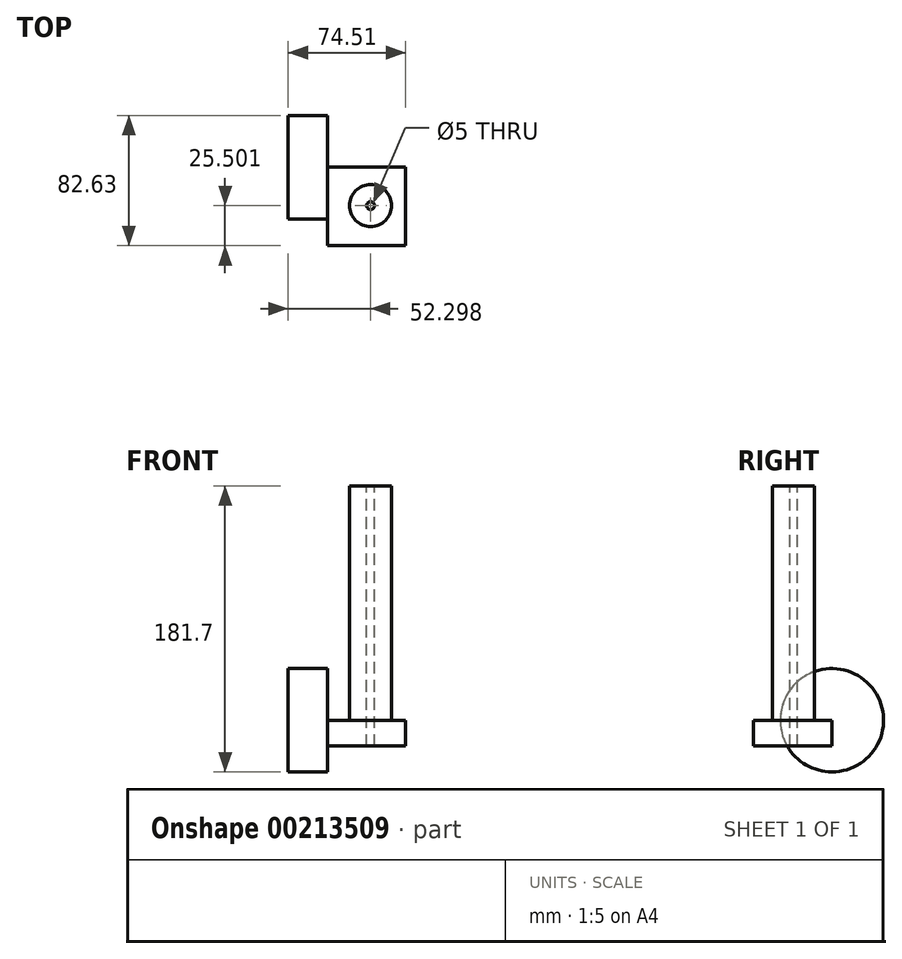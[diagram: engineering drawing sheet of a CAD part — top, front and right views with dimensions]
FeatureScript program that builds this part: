
annotation { "Feature Type Name" : "Feature", "Feature Type Description" : "" }
export const myFeature = defineFeature(function(context is Context, id is Id, definition is map)
    precondition{}
    {
        {
            var Q0;
            Q0=qCreatedBy(makeId("Right.planeOp"),FACE);
            var sketch = newSketch(context, id + "F0", { "sketchPlane" : qUnion([Q0])});
            skCircle(sketch, "E0", {"center": v(-28.06, 48.43) * mm, "radius": 32.8 * mm});
            skSolve(sketch);
        }
        {
            var Q0;
            Q0 = qSketchRegion(id + "F0", true);
            extrude(context, id + "F1", {"entities" : qUnion([Q0]), "depth" : 25 * mm});
        }
        {
            var Q0;
            Q0=makeQuery(id+"F1.opExtrude","CAP_FACE",FACE,{"disambiguationData":[OSD([sQuery(id+"F0.wireOp",EDGE,"E0")])],"isStart":false});
            var sketch = newSketch(context, id + "F2", { "sketchPlane" : qUnion([Q0])});
            skLineSegment(sketch, "E1.bottom", {"start": v(-28.06, 48.43) * mm, "end": v(-77.88, 48.43) * mm});
            skLineSegment(sketch, "E1.top", {"start": v(-28.06, 32) * mm, "end": v(-77.88, 32) * mm});
            skLineSegment(sketch, "E1.left", {"start": v(-28.06, 48.43) * mm, "end": v(-28.06, 32) * mm});
            skLineSegment(sketch, "E1.right", {"start": v(-77.88, 48.43) * mm, "end": v(-77.88, 32) * mm});
            skSolve(sketch);
        }
        {
            var Q0;
            Q0 = qSketchRegion(id + "F2", true);
            extrude(context, id + "F3", {"entities" : qUnion([Q0]), "depth" : 49.5 * mm});
        }
        {
            var Q0;
            Q0=makeQuery(id+"F3.opExtrude","SWEPT_FACE",FACE,{"disambiguationData":[OSD([sQuery(id+"F2.wireOp",EDGE,"E1.bottom")])]});
            var sketch = newSketch(context, id + "F7", { "sketchPlane" : qUnion([Q0])});
            skCircle(sketch, "E2", {"center": v(52.3, -52.38) * mm, "radius": 13.33 * mm});
            skSolve(sketch);
        }
        {
            var Q0;
            Q0=makeQuery(id+"F7.imprint","IMPRINT",FACE,{"disambiguationData":[TD([[makeQuery(id+"F7.imprint","IMPRINT",EDGE,{"derivedFrom":sQuery(id+"F7.wireOp",EDGE,"E2")}),1.0]])]});
            extrude(context, id + "F4", {"entities" : qUnion([Q0]), "operationType" : NewBodyOperationType.ADD, "depth" : 148.9 * mm});
        }
        {
            var Q0;
            Q0=makeQuery(id+"F4.opExtrude","CAP_FACE",FACE,{"disambiguationData":[OSD([sQuery(id+"F7.wireOp",EDGE,"E2")])],"isStart":false});
            var sketch = newSketch(context, id + "F5", { "sketchPlane" : qUnion([Q0])});
            skPoint(sketch, "E3", {"position": v(52.3, -52.38) * mm});
            skSolve(sketch);
        }
        {
            var Q0;
            Q0=sQuery(id+"F5.wireOp",VERTEX,"E3");
            var Q1;
            Q1=makeQuery(id+"F3.opExtrude","SWEPT_BODY",BODY,{"disambiguationData":[OSD([sQuery(id+"F2.wireOp",EDGE,"E1.bottom"),sQuery(id+"F2.wireOp",EDGE,"E1.top"),sQuery(id+"F2.wireOp",EDGE,"E1.left"),sQuery(id+"F2.wireOp",EDGE,"E1.right")])]});
            hole(context, id + "F8", {"style" : HoleStyle.SIMPLE, "endStyle" : HoleEndStyle.THROUGH, "holeDiameter" : 5 * mm, "locations" : qUnion([Q0]), "scope" : qUnion([Q1]), "isTappedThrough" : true});
        }
        {
            var Q0;
            Q0=makeQuery(id+"F3.opExtrude","CAP_FACE",FACE,{"disambiguationData":[OSD([sQuery(id+"F2.wireOp",EDGE,"E1.bottom"),sQuery(id+"F2.wireOp",EDGE,"E1.top"),sQuery(id+"F2.wireOp",EDGE,"E1.left"),sQuery(id+"F2.wireOp",EDGE,"E1.right")])],"isStart":false});
            var sketch = newSketch(context, id + "F9", { "sketchPlane" : qUnion([Q0])});
            skArc(sketch, "E4", {"start": v(67.3, 33.24) * mm, "mid": v(65.65, 113.48) * mm, "end": v(30.65, 41.26) * mm});
            skArc(sketch, "E5", {"start": v(34.73, 40.85) * mm, "mid": v(59.42, 55.65) * mm, "end": v(30.65, 54.56) * mm});
            skSolve(sketch);
        }
        {
            var Q0;
            Q0=sQuery(id+"F9.wireOp",EDGE,"E4");
            extrude(context, id + "F6", {"bodyType" : ToolBodyType.SURFACE, "surfaceEntities" : qUnion([Q0]), "depth" : 25 * mm});
        }
    });
